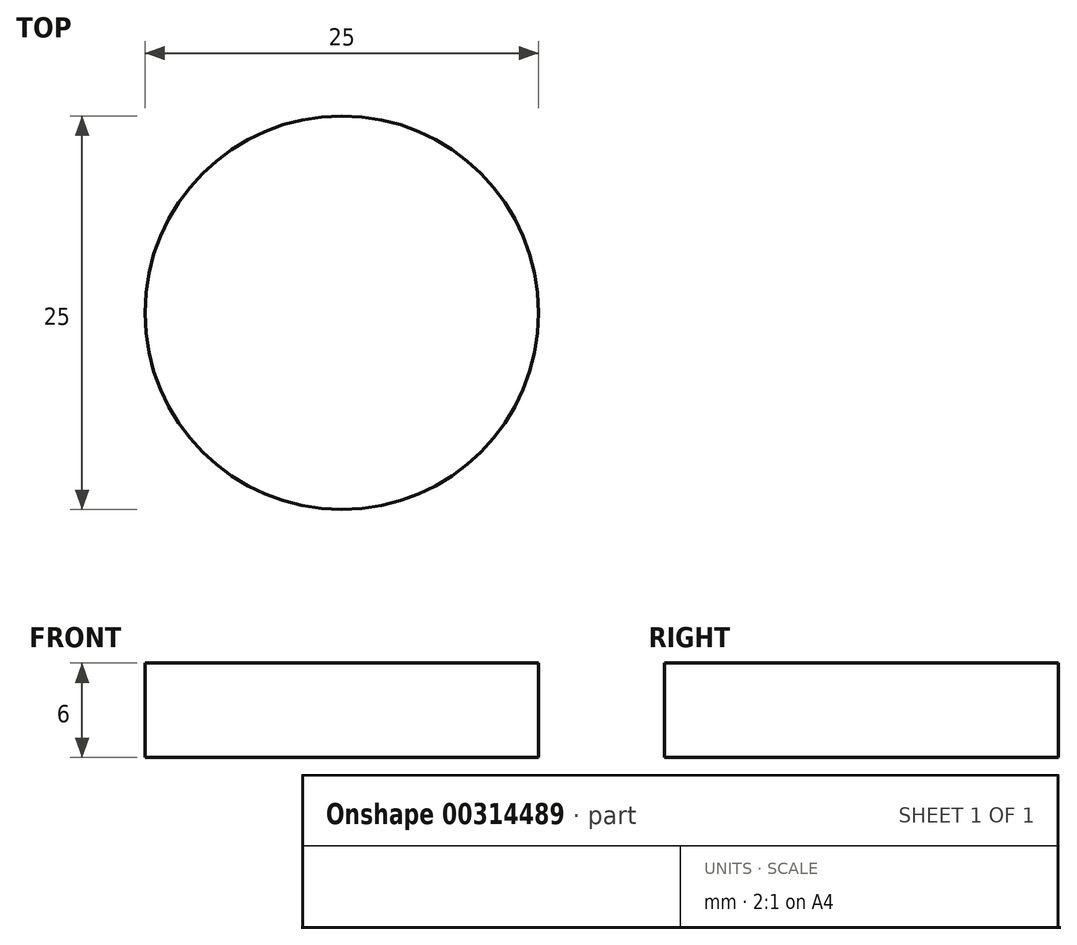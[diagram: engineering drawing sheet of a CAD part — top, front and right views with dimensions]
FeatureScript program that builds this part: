
annotation { "Feature Type Name" : "Feature", "Feature Type Description" : "" }
export const myFeature = defineFeature(function(context is Context, id is Id, definition is map)
    precondition{}
    {
        {
            var Q0;
            Q0=qCreatedBy(makeId("Top.planeOp"),FACE);
            var sketch = newSketch(context, id + "F0", { "sketchPlane" : qUnion([Q0])});
            skCircle(sketch, "E0", {"center": v(-19.25, 0) * mm, "radius": 12.5 * mm});
            skLineSegment(sketch, "E1", {"start": v(-36.35, -14.4) * mm, "end": v(-33.85, -11.9) * mm});
            skLineSegment(sketch, "E2", {"start": v(-34.15, -16.6) * mm, "end": v(-31.65, -14.1) * mm});
            skArc(sketch, "E3", {"start": v(-31.65, -14.1) * mm, "mid": v(-31.65, -11.9) * mm, "end": v(-33.85, -11.9) * mm});
            skArc(sketch, "E4", {"start": v(-36.35, -14.4) * mm, "mid": v(-36.35, -16.6) * mm, "end": v(-34.15, -16.6) * mm});
            skLineSegment(sketch, "E5", {"start": v(-33.85, 11.9) * mm, "end": v(-36.35, 14.4) * mm});
            skLineSegment(sketch, "E6", {"start": v(-31.65, 14.1) * mm, "end": v(-34.15, 16.6) * mm});
            skArc(sketch, "E7", {"start": v(-34.15, 16.6) * mm, "mid": v(-36.35, 16.6) * mm, "end": v(-36.35, 14.4) * mm});
            skArc(sketch, "E8", {"start": v(-33.85, 11.9) * mm, "mid": v(-31.65, 11.9) * mm, "end": v(-31.65, 14.1) * mm});
            skLineSegment(sketch, "E9", {"start": v(-5.35, -16.6) * mm, "end": v(-7.85, -14.1) * mm});
            skLineSegment(sketch, "E10", {"start": v(-3.15, -14.4) * mm, "end": v(-5.65, -11.9) * mm});
            skArc(sketch, "E11", {"start": v(-5.65, -11.9) * mm, "mid": v(-7.85, -11.9) * mm, "end": v(-7.85, -14.1) * mm});
            skArc(sketch, "E12", {"start": v(-5.35, -16.6) * mm, "mid": v(-3.15, -16.6) * mm, "end": v(-3.15, -14.4) * mm});
            skLineSegment(sketch, "E13", {"start": v(-3.15, 14.4) * mm, "end": v(-5.65, 11.9) * mm});
            skLineSegment(sketch, "E14", {"start": v(-5.35, 16.6) * mm, "end": v(-7.85, 14.1) * mm});
            skArc(sketch, "E15", {"start": v(-7.85, 14.1) * mm, "mid": v(-7.85, 11.9) * mm, "end": v(-5.65, 11.9) * mm});
            skArc(sketch, "E16", {"start": v(-3.15, 14.4) * mm, "mid": v(-3.15, 16.6) * mm, "end": v(-5.35, 16.6) * mm});
            skCircle(sketch, "E17", {"center": v(12.8, 10) * mm, "radius": 2.55 * mm});
            skCircle(sketch, "E18", {"center": v(32.8, 10) * mm, "radius": 2.55 * mm});
            skCircle(sketch, "E19", {"center": v(32.8, 0) * mm, "radius": 2.55 * mm});
            skCircle(sketch, "E20", {"center": v(12.8, 0) * mm, "radius": 2.55 * mm});
            skCircle(sketch, "E21", {"center": v(12.8, -10) * mm, "radius": 2.55 * mm});
            skCircle(sketch, "E22", {"center": v(32.8, -10) * mm, "radius": 2.55 * mm});
            skArc(sketch, "E23", {"start": v(-38, 19.75) * mm, "mid": v(-40.12, 18.87) * mm, "end": v(-41, 16.75) * mm});
            skLineSegment(sketch, "E24", {"start": v(-41, -16.75) * mm, "end": v(-41, 16.75) * mm});
            skArc(sketch, "E25", {"start": v(-41, -16.75) * mm, "mid": v(-40.12, -18.87) * mm, "end": v(-38, -19.75) * mm});
            skLineSegment(sketch, "E26", {"start": v(38, -19.75) * mm, "end": v(-38, -19.75) * mm});
            skArc(sketch, "E27", {"start": v(38, -19.75) * mm, "mid": v(40.12, -18.87) * mm, "end": v(41, -16.75) * mm});
            skLineSegment(sketch, "E28", {"start": v(41, 16.75) * mm, "end": v(41, -16.75) * mm});
            skLineSegment(sketch, "E29", {"start": v(38, 19.75) * mm, "end": v(-38, 19.75) * mm});
            skArc(sketch, "E30", {"start": v(41, 16.75) * mm, "mid": v(40.12, 18.87) * mm, "end": v(38, 19.75) * mm});
            skSolve(sketch);
        }
        {
            var Q0;
            Q0=makeQuery(id+"F0.imprint","IMPRINT",FACE,{"disambiguationData":[TD([[makeQuery(id+"F0.imprint","IMPRINT",EDGE,{"derivedFrom":sQuery(id+"F0.wireOp",EDGE,"E0")}),1.0]])]});
            extrude(context, id + "F1", {"entities" : qUnion([Q0]), "depth" : 6 * mm});
        }
    });
